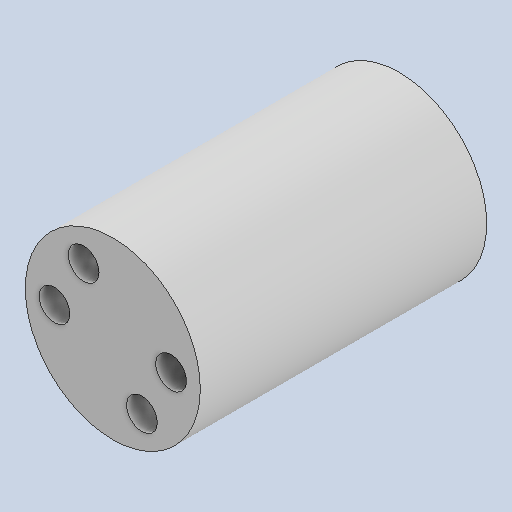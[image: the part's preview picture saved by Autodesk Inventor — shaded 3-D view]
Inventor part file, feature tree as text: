
AUTODESK INVENTOR PART (.ipt)
format: ipt  version: 2023 (Build 270158000, 158)  size: 224,256 bytes
history: native  units: in
note: dims shown in document units (in); Inventor stores cm internally (conversion verified against a paired STEP export)
features: extrude x1, sketch x1
ambient origin geometry x8: Origin, YZ Plane, XZ Plane, XY Plane, X Axis, Y Axis, Z Axis, Center Point
bodies: Body1 (feature_tree)
feature tree (2):
  extrude  "Extrusion14"  Depth=1.228in
  sketch  "Sketch1"  dims[d3=0.866in d15=0.75in d37=0.75in d69=0.132in d70=0.132in d73=1.228in d74=0.0in d75=0.132in d76=0.132in d77=0.132in d78=0.132in]
